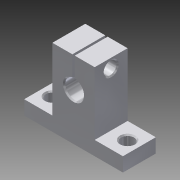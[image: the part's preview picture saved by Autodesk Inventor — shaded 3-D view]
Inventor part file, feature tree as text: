
AUTODESK INVENTOR PART (.ipt)
format: ipt  version: 2015 SP1 (Build 190203100, 203)  size: 147,968 bytes
history: native  units: mm
features: extrude x3, sketch x3, projected_geometry x3, chamfer x1
ambient origin geometry x8: Origin, YZ Plane, XZ Plane, XY Plane, X Axis, Y Axis, Z Axis, Center Point
bodies: Solid1 (feature_tree)
feature tree (10):
  extrude  "Extrusion1"  Depth=6.0mm
  extrude  "Extrusion2"  Depth=32.8mm
  extrude  "Extrusion3"  Depth=18.0mm
  chamfer  "Chamfer1"  Distance=8.0mm
  sketch  "Sketch1"  dims[d0=42.0mm d1=6.0mm]
  sketch  "Sketch2"  dims[d2=20.0mm d3=32.8mm]
  projected_geometry  "Projected Loop1"
  projected_geometry  "Projected Loop2"
  sketch  "Sketch3"  dims[d4=21.0mm d5=18.0mm d6=8.0mm d7=1.0mm d8=14.0mm d9=0.0mm d10=5.5mm d11=32.0mm d12=14.0mm d13=0.0mm d14=5.5mm d15=4.0mm d16=14.0mm d17=0.0mm d18=0.5mm d19=2.0mm d20=45.0deg d21=5.0mm]
  projected_geometry  "Projected Loop3"
